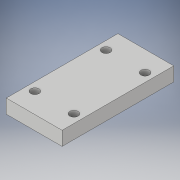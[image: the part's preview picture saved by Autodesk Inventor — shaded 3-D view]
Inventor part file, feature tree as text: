
AUTODESK INVENTOR PART (.ipt)
format: ipt  version: 2019 (Build 230136000, 136)  size: 111,616 bytes
history: native  units: in
note: dims shown in document units (in); Inventor stores cm internally (conversion verified against a paired STEP export)
features: sketch x2, extrude x1, hole x1, projected_geometry x1
ambient origin geometry x8: Origin, YZ Plane, XZ Plane, XY Plane, X Axis, Y Axis, Z Axis, Center Point
bodies: Solid1 (feature_tree)
feature tree (5):
  extrude  "Extrusion1"  Depth=1.0in
  hole  "Hole1"  [1 undecoded]
  sketch  "Sketch1"  dims[d0=2.0in d1=1.0in]
  sketch  "Sketch2"  dims[d2=0.25in d3=0.0in d4=1.275in d5=2.0in d6=0.3625in d9=1.275in d10=0.15in d11=0.15in d12=0.15in d13=0.15in d14=0.3625in d15=0.15in d16=0.75in d17=0.375in d18=0.25in d19=0.5635in d20=1.0in d21=0.8108in]
  projected_geometry  "Projected Loop1"
note: 1 required parameter value undecoded (feature->parameter linkage not recoverable at this tier; creation-order binding heuristic only, values carry confidence <= 0.55)
